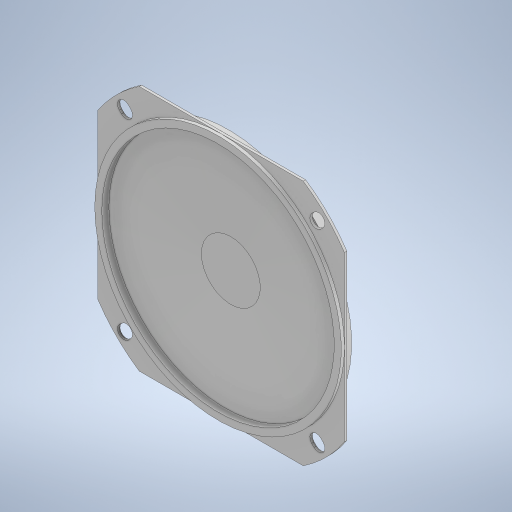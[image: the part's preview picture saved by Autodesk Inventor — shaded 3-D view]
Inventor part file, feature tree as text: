
AUTODESK INVENTOR PART (.ipt)
format: ipt  version: 2023.1 (Build 271208000, 208)  size: 351,744 bytes
history: native  units: mm
features: sketch x4, revolve x3, extrude x2, other x1, pattern_circular x1
ambient origin geometry x8: Origin, YZ Plane, XZ Plane, XY Plane, X Axis, Y Axis, Z Axis, Center Point
bodies: Body1 (feature_tree)
feature tree (11):
  other  "솔리드1"
  extrude  "돌출1"  Depth=92.5mm
  revolve  "회전1"
  sketch  "스케치3"
  revolve  "회전2"
  revolve  "회전3"
  extrude  "돌출2"  Depth=77.0mm
  pattern_circular  "원형 패턴1"  [2 undecoded]
  sketch  "스케치1"
  sketch  "스케치2"
  sketch  "스케치4"
note: 2 required parameter values undecoded (feature->parameter linkage not recoverable at this tier; creation-order binding heuristic only, values carry confidence <= 0.55)
